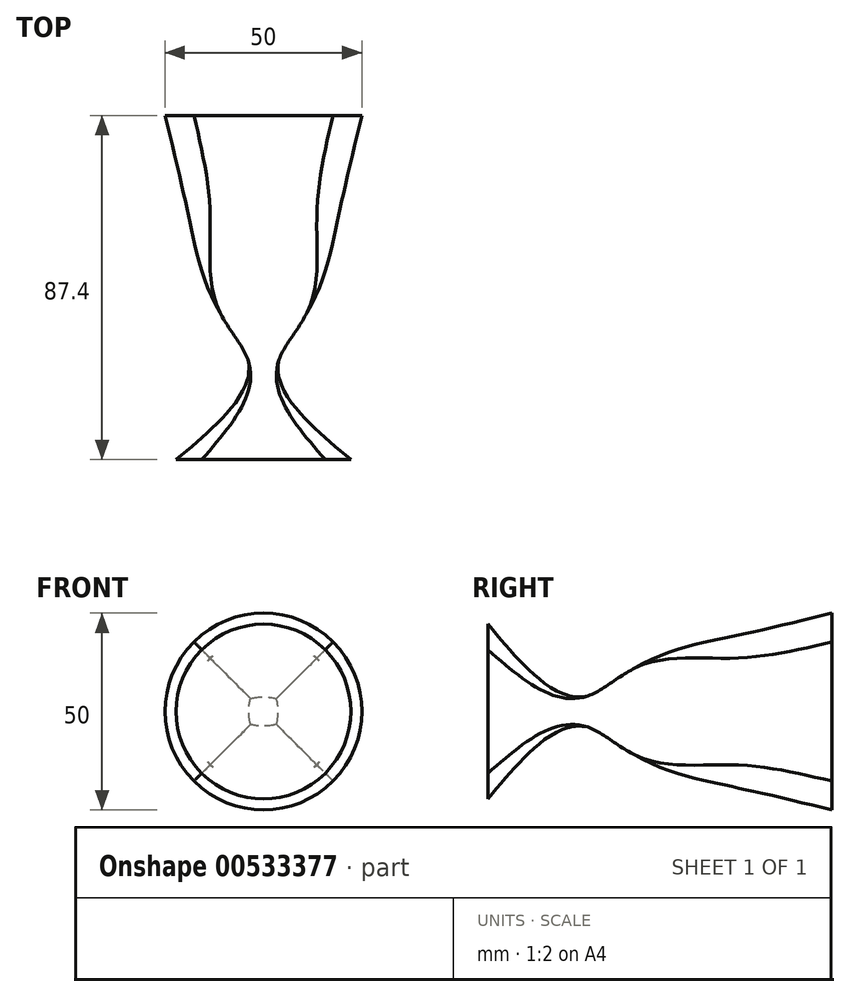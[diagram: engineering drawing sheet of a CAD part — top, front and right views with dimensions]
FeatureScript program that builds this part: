
annotation { "Feature Type Name" : "Feature", "Feature Type Description" : "" }
export const myFeature = defineFeature(function(context is Context, id is Id, definition is map)
    precondition{}
    {
        {
            var Q0;
            Q0=qCreatedBy(makeId("Front.planeOp"),FACE);
            var sketch = newSketch(context, id + "F0", { "sketchPlane" : qUnion([Q0])});
            skCircle(sketch, "E0", {"center": v(0, 0) * mm, "radius": 25 * mm});
            skSolve(sketch);
        }
        {
            var Q0;
            Q0=qCreatedBy(makeId("Front.planeOp"),FACE);
            cPlane(context, id + "F1", {"entities" : qUnion([Q0]), "cplaneType" : CPlaneType.OFFSET, "offset" : 25 * mm, "width" : 152.4 * mm, "height" : 152.4 * mm});
        }
        {
            var Q0;
            Q0=qCreatedBy(id+"F1.planeOp",FACE);
            var sketch = newSketch(context, id + "F2", { "sketchPlane" : qUnion([Q0])});
            skCircle(sketch, "E1", {"center": v(0, 0) * mm, "radius": 19.17 * mm});
            skSolve(sketch);
        }
        {
            var Q0;
            Q0=qCreatedBy(id+"F1.planeOp",FACE);
            cPlane(context, id + "F3", {"entities" : qUnion([Q0]), "cplaneType" : CPlaneType.OFFSET, "offset" : 25 * mm, "width" : 152.4 * mm, "height" : 152.4 * mm});
        }
        {
            var Q0;
            Q0=qCreatedBy(id+"F3.planeOp",FACE);
            var sketch = newSketch(context, id + "F4", { "sketchPlane" : qUnion([Q0])});
            skLineSegment(sketch, "E2.bottom", {"start": v(11.04, 11.04) * mm, "end": v(-11.04, 11.04) * mm});
            skLineSegment(sketch, "E2.top", {"start": v(11.04, -11.04) * mm, "end": v(-11.04, -11.04) * mm});
            skLineSegment(sketch, "E2.left", {"start": v(11.04, 11.04) * mm, "end": v(11.04, -11.04) * mm});
            skLineSegment(sketch, "E2.right", {"start": v(-11.04, 11.04) * mm, "end": v(-11.04, -11.04) * mm});
            skPoint(sketch, "E2.middle", {"position": v(0, 0) * mm});
            skSolve(sketch);
        }
        {
            var Q0;
            Q0=qCreatedBy(id+"F3.planeOp",FACE);
            cPlane(context, id + "F5", {"entities" : qUnion([Q0]), "cplaneType" : CPlaneType.OFFSET, "offset" : 12 * mm, "width" : 152.4 * mm, "height" : 152.4 * mm});
        }
        {
            var Q0;
            Q0=qCreatedBy(id+"F5.planeOp",FACE);
            var sketch = newSketch(context, id + "F6", { "sketchPlane" : qUnion([Q0])});
            skLineSegment(sketch, "E3.bottom", {"start": v(3.97, 3.97) * mm, "end": v(-3.97, 3.97) * mm});
            skLineSegment(sketch, "E3.top", {"start": v(3.97, -3.97) * mm, "end": v(-3.97, -3.97) * mm});
            skLineSegment(sketch, "E3.left", {"start": v(3.97, 3.97) * mm, "end": v(3.97, -3.97) * mm});
            skLineSegment(sketch, "E3.right", {"start": v(-3.97, 3.97) * mm, "end": v(-3.97, -3.97) * mm});
            skPoint(sketch, "E3.middle", {"position": v(0, 0) * mm});
            skSolve(sketch);
        }
        {
            var Q0;
            Q0=qCreatedBy(id+"F5.planeOp",FACE);
            cPlane(context, id + "F7", {"entities" : qUnion([Q0]), "cplaneType" : CPlaneType.OFFSET, "offset" : 25.4 * mm, "width" : 152.4 * mm, "height" : 152.4 * mm});
        }
        {
            var Q0;
            Q0=qCreatedBy(id+"F7.planeOp",FACE);
            var sketch = newSketch(context, id + "F8", { "sketchPlane" : qUnion([Q0])});
            skCircle(sketch, "E4", {"center": v(0, 0) * mm, "radius": 22.2 * mm});
            skSolve(sketch);
        }
        {
            var Q0;
            Q0=makeQuery(id+"F0.imprint","IMPRINT",FACE,{"disambiguationData":[TD([[makeQuery(id+"F0.imprint","IMPRINT",EDGE,{"derivedFrom":sQuery(id+"F0.wireOp",EDGE,"E0")}),1.0]])]});
            var Q1;
            Q1=makeQuery(id+"F2.imprint","IMPRINT",FACE,{"disambiguationData":[TD([[makeQuery(id+"F2.imprint","IMPRINT",EDGE,{"derivedFrom":sQuery(id+"F2.wireOp",EDGE,"E1")}),1.0]])]});
            var Q2;
            Q2=makeQuery(id+"F4.imprint","IMPRINT",FACE,{"disambiguationData":[TD([[makeQuery(id+"F4.imprint","IMPRINT",EDGE,{"derivedFrom":sQuery(id+"F4.wireOp",EDGE,"E2.bottom")}),1.0]])]});
            var Q3;
            Q3=makeQuery(id+"F6.imprint","IMPRINT",FACE,{"disambiguationData":[TD([[makeQuery(id+"F6.imprint","IMPRINT",EDGE,{"derivedFrom":sQuery(id+"F6.wireOp",EDGE,"E3.bottom")}),1.0]])]});
            var Q4;
            Q4=makeQuery(id+"F8.imprint","IMPRINT",FACE,{"disambiguationData":[TD([[makeQuery(id+"F8.imprint","IMPRINT",EDGE,{"derivedFrom":sQuery(id+"F8.wireOp",EDGE,"E4")}),1.0]])]});
            loft(context, id + "F9", {"sheetProfilesArray" : [{ "sheetProfileEntities" : qUnion([Q0]) }, { "sheetProfileEntities" : qUnion([Q1]) }, { "sheetProfileEntities" : qUnion([Q2]) }, { "sheetProfileEntities" : qUnion([Q3]) }, { "sheetProfileEntities" : qUnion([Q4]) }]});
        }
    });
